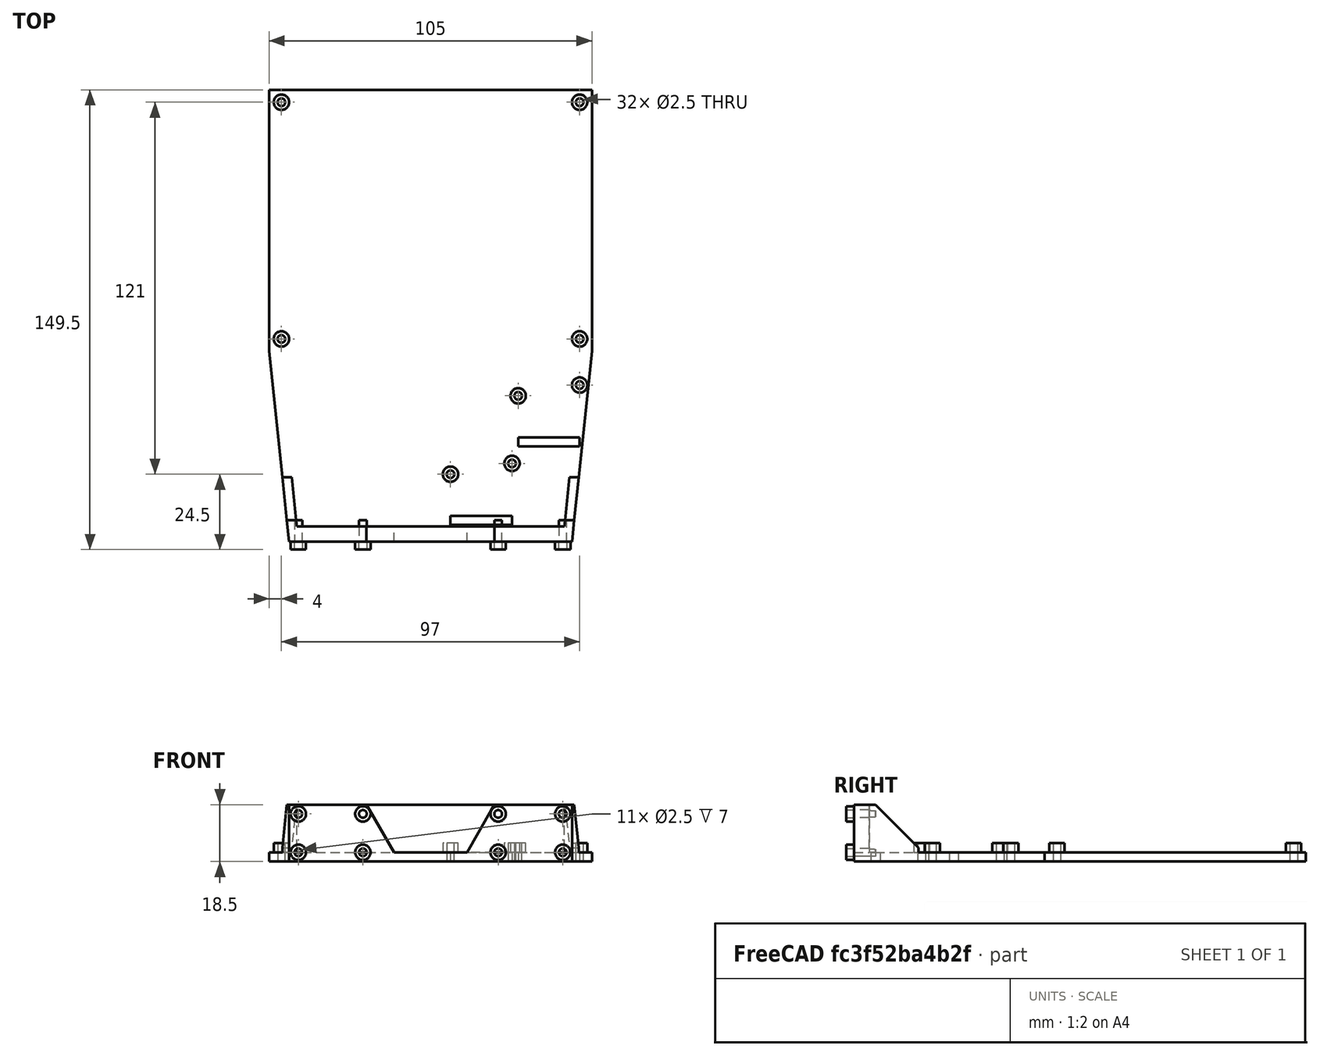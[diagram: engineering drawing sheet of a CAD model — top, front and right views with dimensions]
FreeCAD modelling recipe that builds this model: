
FCSTD DOCUMENT  (FreeCAD 0.17R8469 (Git))
Label: StereoVisionTest
License: All rights reserved
LicenseURL: http://en.wikipedia.org/wiki/All_rights_reserved
objects: Sketcher::SketchObject×7, PartDesign::Pad×4, PartDesign::Pocket×3, PartDesign::Chamfer×2, PartDesign::Body×2, App::Part×1
note: 25 computed .brp shape members not serialized (recipe doc carries the construction recipe); baked Part::Feature solids carry a one-line shape summary decoded from their .brp

FEATURE [Sketcher::SketchObject] Sketch
  MapMode = 5
  Support = -> [XY_Plane]
  sketch-geometry (36):
    g0: LineSegment StartX=0 StartY=0 StartZ=0 EndX=105 EndY=0 EndZ=0
    g1: LineSegment StartX=105 StartY=0 StartZ=0 EndX=105 EndY=-85 EndZ=0
    g2: LineSegment StartX=0 StartY=-85 StartZ=0 EndX=0 EndY=0 EndZ=0
    g3: LineSegment StartX=6.5 StartY=-147 StartZ=0 EndX=98.5 EndY=-147 EndZ=0
    g4: LineSegment StartX=6.5 StartY=-147 StartZ=0 EndX=0 EndY=-85 EndZ=0
    g5: LineSegment StartX=98.5 StartY=-147 StartZ=0 EndX=105 EndY=-85 EndZ=0
    g6: LineSegment [constr] StartX=105 StartY=-85 StartZ=0 EndX=0 EndY=-85 EndZ=0
    g7: LineSegment [constr] StartX=6.5 StartY=-85 StartZ=0 EndX=6.5 EndY=-147 EndZ=0
    g8: Circle CenterX=4 CenterY=-4 CenterZ=0 NormalX=0 NormalY=0 NormalZ=1 Radius=1.25
    g9: Circle CenterX=101 CenterY=-4 CenterZ=0 NormalX=0 NormalY=0 NormalZ=1 Radius=1.25
    g10: Circle CenterX=4 CenterY=-81 CenterZ=0 NormalX=0 NormalY=0 NormalZ=1 Radius=1.25
    g11: Circle CenterX=101 CenterY=-81 CenterZ=0 NormalX=0 NormalY=0 NormalZ=1 Radius=1.25
    g12: Circle CenterX=59 CenterY=-125 CenterZ=0 NormalX=0 NormalY=0 NormalZ=1 Radius=1.25
    g13: Circle CenterX=79 CenterY=-121.5 CenterZ=0 NormalX=0 NormalY=0 NormalZ=1 Radius=1.25
    g14: Circle CenterX=81 CenterY=-99.5 CenterZ=0 NormalX=0 NormalY=0 NormalZ=1 Radius=1.25
    g15: Circle CenterX=101 CenterY=-96 CenterZ=0 NormalX=0 NormalY=0 NormalZ=1 Radius=1.25
    g16: LineSegment [constr] StartX=4 StartY=-4 StartZ=0 EndX=101 EndY=-4 EndZ=0
    g17: LineSegment [constr] StartX=101 StartY=-4 StartZ=0 EndX=101 EndY=-81 EndZ=0
    g18: LineSegment [constr] StartX=101 StartY=-81 StartZ=0 EndX=4 EndY=-81 EndZ=0
    g19: LineSegment [constr] StartX=4 StartY=-81 StartZ=0 EndX=4 EndY=-4 EndZ=0
    g20: LineSegment [constr] StartX=59 StartY=-125 StartZ=0 EndX=79 EndY=-125 EndZ=0
    g21: LineSegment [constr] StartX=79 StartY=-125 StartZ=0 EndX=79 EndY=-121.5 EndZ=0
    g22: LineSegment [constr] StartX=79 StartY=-121.5 StartZ=0 EndX=59 EndY=-121.5 EndZ=0
    g23: LineSegment [constr] StartX=59 StartY=-121.5 StartZ=0 EndX=59 EndY=-125 EndZ=0
    g24: LineSegment [constr] StartX=81 StartY=-99.5 StartZ=0 EndX=101 EndY=-99.5 EndZ=0
    g25: LineSegment [constr] StartX=101 StartY=-99.5 StartZ=0 EndX=101 EndY=-96 EndZ=0
    g26: LineSegment [constr] StartX=101 StartY=-96 StartZ=0 EndX=81 EndY=-96 EndZ=0
    g27: LineSegment [constr] StartX=81 StartY=-96 StartZ=0 EndX=81 EndY=-99.5 EndZ=0
    g28: LineSegment [constr] StartX=0 StartY=0 StartZ=0 EndX=4 EndY=-4 EndZ=0
    g29: LineSegment [constr] StartX=105 StartY=0 StartZ=0 EndX=101 EndY=-4 EndZ=0
    g30: LineSegment [constr] StartX=101 StartY=-81 StartZ=0 EndX=101 EndY=-96 EndZ=0
    g31: LineSegment [constr] StartX=81 StartY=-99.5 StartZ=0 EndX=79 EndY=-99.5 EndZ=0
    g32: LineSegment [constr] StartX=79 StartY=-99.5 StartZ=0 EndX=79 EndY=-121.5 EndZ=0
    g33: LineSegment [constr] StartX=79 StartY=-121.5 StartZ=0 EndX=81 EndY=-121.5 EndZ=0
    g34: LineSegment [constr] StartX=81 StartY=-121.5 StartZ=0 EndX=81 EndY=-99.5 EndZ=0
    g35: LineSegment [constr] StartX=59 StartY=-125 StartZ=0 EndX=59 EndY=-147 EndZ=0
  constraints (89):
    c: Coincident(g0,g1)
    c: Coincident(g2,g0)
    c: Horizontal(g0)
    c: Vertical(g1)
    c: Vertical(g2)
    c: DistanceX(g0,g0) = 105
    c: DistanceY(g1,g1) = 85
    c: Coincident(g0,g-1)
    c: Horizontal(g3)
    c: DistanceX(g3,g3) = 92
    c: Coincident(g4,g3)
    c: Coincident(g5,g3)
    c: Coincident(g5,g1)
    c: Equal(g5,g4)
    c: Coincident(g4,g2)
    c: Coincident(g6,g1)
    c: Coincident(g6,g2)
    c: Horizontal(g6)
    c: PointOnObject(g7,g6)
    c: PointOnObject(g7,g3)
    c: Vertical(g7)
    c: Coincident(g3,g7)
    c: Radius(g8) = 1.25
    c: Equal(g8, g10-g15) x6
    c: Equal(g8,g9)
    c: Coincident(g16,g17)
    c: Coincident(g17,g18)
    c: Coincident(g18,g19)
    c: Coincident(g19,g16)
    c: Horizontal(g16)
    c: Horizontal(g18)
    c: Vertical(g17)
    c: Vertical(g19)
    c: Coincident(g20,g21)
    c: Coincident(g21,g22)
    c: Coincident(g22,g23)
    c: Coincident(g23,g20)
    c: Horizontal(g20)
    c: Horizontal(g22)
    c: Vertical(g21)
    c: Vertical(g23)
    c: Coincident(g24,g25)
    c: Coincident(g25,g26)
    c: Coincident(g26,g27)
    c: Coincident(g27,g24)
    c: Horizontal(g24)
    c: Horizontal(g26)
    c: Vertical(g25)
    c: Vertical(g27)
    c: Coincident(g8,g16)
    c: Coincident(g10,g18)
    c: Coincident(g9,g16)
    c: Coincident(g17,g11)
    c: Coincident(g20,g12)
    c: Coincident(g13,g21)
    c: Coincident(g24,g14)
    c: Coincident(g25,g15)
    c: Equal(g26,g22)
    c: Equal(g25,g21)
    c: DistanceX(g22,g22) = 20
    c: DistanceY(g21,g21) = 3.5
    c: DistanceY(g17,g17) = 77
    c: DistanceX(g18,g18) = 97
    c: Coincident(g28,g-1)
    c: Coincident(g28,g8)
    c: Coincident(g29,g0)
    c: Coincident(g29,g9)
    c: Equal(g29,g28)
    c: Angle(g28) = -0.785398
    c: Coincident(g30,g11)
    c: Coincident(g30,g15)
    c: Vertical(g30)
    c: Distance(g30) = 15
    c: Coincident(g31,g32)
    c: Coincident(g32,g33)
    c: Coincident(g33,g34)
    c: Coincident(g34,g31)
    c: Horizontal(g31)
    c: Horizontal(g33)
    c: Vertical(g32)
    c: Vertical(g34)
    c: Coincident(g31,g14)
    c: Coincident(g32,g13)
    c: Distance(g34) = 22
    c: Distance(g31) = 2
    c: Coincident(g35,g12)
    c: PointOnObject(g35,g3)
    c: Vertical(g35)
    c: Distance(g35) = 22
FEATURE [PartDesign::Pad] Pad
  Length = 3
  Length2 = 100
  Profile = -> Sketch
  Type = 0
FEATURE [Sketcher::SketchObject] Sketch001
  ExternalGeometry = -> [Pad]
  MapMode = 5
  Placement = pos=(0,0,3) rot=(0,0,1;0rad)
  Support = -> [Pad]
  sketch-geometry (16):
    g0: Circle CenterX=4 CenterY=-4 CenterZ=0 NormalX=0 NormalY=0 NormalZ=1 Radius=2.5
    g1: Circle CenterX=101 CenterY=-81 CenterZ=0 NormalX=0 NormalY=0 NormalZ=1 Radius=2.5
    g2: Circle CenterX=101 CenterY=-4 CenterZ=0 NormalX=0 NormalY=0 NormalZ=1 Radius=2.5
    g3: Circle CenterX=4 CenterY=-81 CenterZ=0 NormalX=0 NormalY=0 NormalZ=1 Radius=2.5
    g4: Circle CenterX=79 CenterY=-121.5 CenterZ=0 NormalX=0 NormalY=0 NormalZ=1 Radius=2.5
    g5: Circle CenterX=59 CenterY=-125 CenterZ=0 NormalX=0 NormalY=0 NormalZ=1 Radius=2.5
    g6: Circle CenterX=81 CenterY=-99.5 CenterZ=0 NormalX=0 NormalY=0 NormalZ=1 Radius=2.5
    g7: Circle CenterX=101 CenterY=-96 CenterZ=0 NormalX=0 NormalY=0 NormalZ=1 Radius=1.25
    g8: Circle CenterX=4 CenterY=-81 CenterZ=0 NormalX=0 NormalY=0 NormalZ=1 Radius=1.25
    g9: Circle CenterX=79 CenterY=-121.5 CenterZ=0 NormalX=0 NormalY=0 NormalZ=1 Radius=1.25
    g10: Circle CenterX=81 CenterY=-99.5 CenterZ=0 NormalX=0 NormalY=0 NormalZ=1 Radius=1.25
    g11: Circle CenterX=101 CenterY=-96 CenterZ=0 NormalX=0 NormalY=0 NormalZ=1 Radius=2.5
    g12: Circle CenterX=59 CenterY=-125 CenterZ=0 NormalX=0 NormalY=0 NormalZ=1 Radius=1.25
    g13: Circle CenterX=101 CenterY=-4 CenterZ=0 NormalX=0 NormalY=0 NormalZ=1 Radius=1.25
    g14: Circle CenterX=4 CenterY=-4 CenterZ=0 NormalX=0 NormalY=0 NormalZ=1 Radius=1.25
    g15: Circle CenterX=101 CenterY=-81 CenterZ=0 NormalX=0 NormalY=0 NormalZ=1 Radius=1.25
  constraints (27):
    c: Coincident(g6,g-8)
    c: Coincident(g7,g-9)
    c: Coincident(g5,g-10)
    c: Coincident(g4,g-7)
    c: Coincident(g3,g-6)
    c: Coincident(g2,g-5)
    c: Coincident(g1,g-3)
    c: Coincident(g0,g-4)
    c: Radius(g0) = 2.5
    c: Equal(g0, g1-g6) x6
    c: Coincident(g8,g3)
    c: Equal(g8,g-6)
    c: Coincident(g9,g4)
    c: Equal(g9,g-7)
    c: Coincident(g10,g6)
    c: Equal(g10,g-8)
    c: Coincident(g11,g7)
    c: Coincident(g12,g5)
    c: Equal(g12,g-10)
    c: Coincident(g13,g2)
    c: Equal(g13,g-5)
    c: Coincident(g14,g0)
    c: Equal(g14,g-4)
    c: Coincident(g15,g1)
    c: Equal(g15,g-3)
    c: Equal(g11,g0)
    c: Equal(g7,g-9)
FEATURE [PartDesign::Pad] Pad001
  BaseFeature = -> Pad
  Length = 3
  Length2 = 100
  Profile = -> Sketch001
  Type = 0
FEATURE [Sketcher::SketchObject] Sketch002
  ExternalGeometry = -> [Pad001]
  MapMode = 5
  Placement = pos=(0,0,3) rot=(0,0,1;0rad)
  Support = -> [Pad001]
  sketch-geometry (13):
    g0: LineSegment StartX=6.5 StartY=-147 StartZ=0 EndX=98.5 EndY=-147 EndZ=0
    g1: LineSegment StartX=98.5 StartY=-147 StartZ=0 EndX=100.702 EndY=-126 EndZ=0
    g2: LineSegment StartX=6.5 StartY=-147 StartZ=0 EndX=4.29839 EndY=-126 EndZ=0
    g3: LineSegment [constr] StartX=4.29839 StartY=-126 StartZ=0 EndX=100.702 EndY=-126 EndZ=0
    g4: LineSegment [constr] StartX=4 StartY=-81 StartZ=0 EndX=4 EndY=-126 EndZ=0
    g5: LineSegment StartX=8.99225 StartY=-142 StartZ=0 EndX=96.0078 EndY=-142 EndZ=0
    g6: LineSegment StartX=96.0078 StartY=-142 StartZ=0 EndX=97.6852 EndY=-126 EndZ=0
    g7: LineSegment StartX=8.99225 StartY=-142 StartZ=0 EndX=7.31483 EndY=-126 EndZ=0
    g8: LineSegment StartX=4.29839 StartY=-126 StartZ=0 EndX=7.31483 EndY=-126 EndZ=0
    g9: LineSegment StartX=97.6852 StartY=-126 StartZ=0 EndX=100.702 EndY=-126 EndZ=0
    g10: LineSegment [constr] StartX=96.0078 StartY=-142 StartZ=0 EndX=98.9914 EndY=-142.313 EndZ=0
    g11: LineSegment [constr] StartX=96.0078 StartY=-142 StartZ=0 EndX=96.0078 EndY=-147 EndZ=0
    g12: LineSegment [constr] StartX=8.99225 StartY=-142 StartZ=0 EndX=6.0086 EndY=-142.313 EndZ=0
  constraints (36):
    c: Coincident(g0,g-5)
    c: Coincident(g0,g-4)
    c: Coincident(g1,g0)
    c: PointOnObject(g1,g-3)
    c: Coincident(g2,g0)
    c: PointOnObject(g2,g-5)
    c: Coincident(g3,g2)
    c: Coincident(g3,g1)
    c: Horizontal(g3)
    c: Coincident(g4,g-6)
    c: PointOnObject(g4,g3)
    c: Vertical(g4)
    c: DistanceY(g4,g4) = 45
    c: Horizontal(g5)
    c: Coincident(g6,g5)
    c: PointOnObject(g6,g3)
    c: Coincident(g7,g5)
    c: PointOnObject(g7,g3)
    c: Parallel(g7,g-5)
    c: Parallel(g6,g-3)
    c: Coincident(g8,g2)
    c: Coincident(g8,g7)
    c: Coincident(g9,g6)
    c: Coincident(g9,g1)
    c: Coincident(g10,g5)
    c: Coincident(g11,g5)
    c: PointOnObject(g11,g-4)
    c: Vertical(g11)
    c: Perpendicular(g-3,g10)
    c: PointOnObject(g10,g-3)
    c: DistanceY(g11,g11) = 5
    c: Distance(g10) = 3
    c: Coincident(g12,g5)
    c: PointOnObject(g12,g-5)
    c: Perpendicular(g-5,g12)
    c: Distance(g12) = 3
FEATURE [PartDesign::Pad] Pad002
  BaseFeature = -> Pad001
  Length = 15.5
  Length2 = 100
  Profile = -> Sketch002
  Type = 0
FEATURE [PartDesign::Chamfer] Chamfer
  Base = -> Pad002 [Edge82]
  BaseFeature = -> Pad002
  Size = 14
FEATURE [PartDesign::Chamfer] Chamfer001
  Base = -> Chamfer [Edge11]
  BaseFeature = -> Chamfer
  Size = 14
FEATURE [Sketcher::SketchObject] Sketch003
  ExternalGeometry = -> [Chamfer001]
  MapMode = 5
  Placement = pos=(0,-147,0) rot=(1,0,0;1.5708rad)
  Support = -> [Chamfer001]
  sketch-geometry (20):
    g0: LineSegment [constr] StartX=9.5 StartY=15.5 StartZ=0 EndX=30.5 EndY=15.5 EndZ=0
    g1: LineSegment [constr] StartX=30.5 StartY=15.5 StartZ=0 EndX=30.5 EndY=3 EndZ=0
    g2: LineSegment [constr] StartX=30.5 StartY=3 StartZ=0 EndX=9.5 EndY=3 EndZ=0
    g3: LineSegment [constr] StartX=9.5 StartY=3 StartZ=0 EndX=9.5 EndY=15.5 EndZ=0
    g4: LineSegment [constr] StartX=74.5 StartY=15.5 StartZ=0 EndX=95.5 EndY=15.5 EndZ=0
    g5: LineSegment [constr] StartX=95.5 StartY=15.5 StartZ=0 EndX=95.5 EndY=3 EndZ=0
    g6: LineSegment [constr] StartX=95.5 StartY=3 StartZ=0 EndX=74.5 EndY=3 EndZ=0
    g7: LineSegment [constr] StartX=74.5 StartY=3 StartZ=0 EndX=74.5 EndY=15.5 EndZ=0
    g8: LineSegment [constr] StartX=30.5 StartY=15.5 StartZ=0 EndX=74.5 EndY=15.5 EndZ=0
    g9: LineSegment [constr] StartX=6.5 StartY=18.5 StartZ=0 EndX=9.5 EndY=15.5 EndZ=0
    g10: LineSegment [constr] StartX=95.5 StartY=15.5 StartZ=0 EndX=98.5 EndY=18.5 EndZ=0
    g11: LineSegment [constr] StartX=9.5 StartY=3 StartZ=0 EndX=9.5 EndY=0 EndZ=0
    g12: Circle CenterX=9.5 CenterY=15.5 CenterZ=0 NormalX=0 NormalY=0 NormalZ=1 Radius=1.25
    g13: Circle CenterX=30.5 CenterY=15.5 CenterZ=0 NormalX=0 NormalY=0 NormalZ=1 Radius=1.25
    g14: Circle CenterX=9.5 CenterY=3 CenterZ=0 NormalX=0 NormalY=0 NormalZ=1 Radius=1.25
    g15: Circle CenterX=30.5 CenterY=3 CenterZ=0 NormalX=0 NormalY=0 NormalZ=1 Radius=1.25
    g16: Circle CenterX=74.5 CenterY=3 CenterZ=0 NormalX=0 NormalY=0 NormalZ=1 Radius=1.25
    g17: Circle CenterX=95.5 CenterY=3 CenterZ=0 NormalX=0 NormalY=0 NormalZ=1 Radius=1.25
    g18: Circle CenterX=95.5 CenterY=15.5 CenterZ=0 NormalX=0 NormalY=0 NormalZ=1 Radius=1.25
    g19: Circle CenterX=74.5 CenterY=15.5 CenterZ=0 NormalX=0 NormalY=0 NormalZ=1 Radius=1.25
  constraints (49):
    c: Coincident(g0,g1)
    c: Coincident(g1,g2)
    c: Coincident(g2,g3)
    c: Coincident(g3,g0)
    c: Horizontal(g0)
    c: Horizontal(g2)
    c: Vertical(g1)
    c: Vertical(g3)
    c: Coincident(g4,g5)
    c: Coincident(g5,g6)
    c: Coincident(g6,g7)
    c: Coincident(g7,g4)
    c: Horizontal(g4)
    c: Horizontal(g6)
    c: Vertical(g5)
    c: Vertical(g7)
    c: Coincident(g8,g0)
    c: Coincident(g8,g4)
    c: Horizontal(g8)
    c: DistanceX(g8,g8) = 44
    c: Equal(g4,g0)
    c: Equal(g5,g1)
    c: DistanceY(g5,g5) = 12.5
    c: DistanceX(g4,g4) = 21
    c: Coincident(g9,g-3)
    c: Coincident(g9,g0)
    c: Coincident(g10,g4)
    c: Coincident(g10,g-3)
    c: Equal(g10,g9)
    c: Coincident(g11,g2)
    c: PointOnObject(g11,g-4)
    c: Vertical(g11)
    c: DistanceY(g11,g11) = 3
    c: Coincident(g12,g0)
    c: Coincident(g13,g0)
    c: Coincident(g14,g2)
    c: Coincident(g15,g1)
    c: Coincident(g16,g6)
    c: Coincident(g17,g5)
    c: Coincident(g18,g4)
    c: Coincident(g19,g4)
    c: Radius(g14) = 1.25
    c: Equal(g14,g12)
    c: Equal(g14,g13)
    c: Equal(g14,g15)
    c: Equal(g14,g16)
    c: Equal(g14,g19)
    c: Equal(g14,g17)
    c: Equal(g14,g18)
FEATURE [PartDesign::Pocket] Pocket
  BaseFeature = -> Chamfer001
  Length = 7
  Profile = -> Sketch003
  Type = 0
FEATURE [Sketcher::SketchObject] Sketch004
  ExternalGeometry = -> [Pocket]
  MapMode = 5
  Placement = pos=(0,-147,0) rot=(1,0,0;1.5708rad)
  Support = -> [Pocket]
  sketch-geometry (16):
    g0: Circle CenterX=9.5 CenterY=15.5 CenterZ=0 NormalX=0 NormalY=0 NormalZ=1 Radius=2.5
    g1: Circle CenterX=30.5 CenterY=15.5 CenterZ=0 NormalX=0 NormalY=0 NormalZ=1 Radius=2.5
    g2: Circle CenterX=74.5 CenterY=15.5 CenterZ=0 NormalX=0 NormalY=0 NormalZ=1 Radius=2.5
    g3: Circle CenterX=95.5 CenterY=15.5 CenterZ=0 NormalX=0 NormalY=0 NormalZ=1 Radius=2.5
    g4: Circle CenterX=95.5 CenterY=3 CenterZ=0 NormalX=0 NormalY=0 NormalZ=1 Radius=2.5
    g5: Circle CenterX=74.5 CenterY=3 CenterZ=0 NormalX=0 NormalY=0 NormalZ=1 Radius=2.5
    g6: Circle CenterX=30.5 CenterY=3 CenterZ=0 NormalX=0 NormalY=0 NormalZ=1 Radius=2.5
    g7: Circle CenterX=9.5 CenterY=3 CenterZ=0 NormalX=0 NormalY=0 NormalZ=1 Radius=2.5
    g8: Circle CenterX=9.5 CenterY=15.5 CenterZ=0 NormalX=0 NormalY=0 NormalZ=1 Radius=1.25
    g9: Circle CenterX=30.5 CenterY=15.5 CenterZ=0 NormalX=0 NormalY=0 NormalZ=1 Radius=1.25
    g10: Circle CenterX=9.5 CenterY=3 CenterZ=0 NormalX=0 NormalY=0 NormalZ=1 Radius=1.25
    g11: Circle CenterX=30.5 CenterY=3 CenterZ=0 NormalX=0 NormalY=0 NormalZ=1 Radius=1.25
    g12: Circle CenterX=74.5 CenterY=15.5 CenterZ=0 NormalX=0 NormalY=0 NormalZ=1 Radius=1.25
    g13: Circle CenterX=74.5 CenterY=3 CenterZ=0 NormalX=0 NormalY=0 NormalZ=1 Radius=1.25
    g14: Circle CenterX=95.5 CenterY=15.5 CenterZ=0 NormalX=0 NormalY=0 NormalZ=1 Radius=1.25
    g15: Circle CenterX=95.5 CenterY=3 CenterZ=0 NormalX=0 NormalY=0 NormalZ=1 Radius=1.25
  constraints (32):
    c: Coincident(g0,g-9)
    c: Coincident(g1,g-10)
    c: Coincident(g2,g-3)
    c: Coincident(g3,g-4)
    c: Coincident(g4,g-5)
    c: Coincident(g5,g-6)
    c: Coincident(g6,g-7)
    c: Coincident(g7,g-8)
    c: Radius(g0) = 2.5
    c: Equal(g0,g1)
    c: Equal(g0,g2)
    c: Equal(g0,g3)
    c: Equal(g0,g6)
    c: Equal(g0,g7)
    c: Equal(g0,g5)
    c: Equal(g0,g4)
    c: Coincident(g8,g0)
    c: Equal(g8,g-9)
    c: Coincident(g9,g1)
    c: Equal(g9,g-10)
    c: Coincident(g10,g7)
    c: Equal(g10,g-8)
    c: Coincident(g11,g6)
    c: Equal(g11,g-7)
    c: Coincident(g12,g2)
    c: Coincident(g13,g5)
    c: Coincident(g14,g3)
    c: Coincident(g15,g4)
    c: Equal(g15,g-5)
    c: Equal(g14,g-4)
    c: Equal(g13,g-6)
    c: Equal(g12,g-3)
FEATURE [PartDesign::Pad] Pad003
  BaseFeature = -> Pocket
  Length = 2.5
  Length2 = 100
  Profile = -> Sketch004
  Type = 0
FEATURE [PartDesign::Body] Body
  Origin = -> BodyOrigin
  Tip = -> Pad003
FEATURE [Sketcher::SketchObject] Sketch005
  ExternalGeometry = -> [Pad003]
  MapMode = 5
  Placement = pos=(0,-147,0) rot=(1,0,0;1.5708rad)
  Support = -> [Pad003]
  sketch-geometry (4):
    g0: LineSegment StartX=31.6547 StartY=18.5 StartZ=0 EndX=40.6036 EndY=3 EndZ=0
    g1: LineSegment StartX=73.3453 StartY=18.5 StartZ=0 EndX=64.3964 EndY=3 EndZ=0
    g2: LineSegment StartX=40.6036 StartY=3 StartZ=0 EndX=64.3964 EndY=3 EndZ=0
    g3: LineSegment StartX=73.3453 StartY=18.5 StartZ=0 EndX=31.6547 EndY=18.5 EndZ=0
  constraints (12):
    c: PointOnObject(g0,g-3)
    c: PointOnObject(g0,g-6)
    c: PointOnObject(g1,g-3)
    c: PointOnObject(g1,g-6)
    c: Coincident(g2,g0)
    c: Coincident(g2,g1)
    c: Coincident(g3,g1)
    c: Coincident(g3,g0)
    c: Tangent(g1,g-5)
    c: Tangent(g0,g-4)
    c: Angle(g1) = -2.0944
    c: Angle(g0) = -1.0472
FEATURE [PartDesign::Pocket] Pocket001
  BaseFeature = -> Pad003
  Length = 5
  Profile = -> Sketch005
  Type = 0
FEATURE [Sketcher::SketchObject] Sketch006
  ExternalGeometry = -> [Pocket001]
  MapMode = 5
  Placement = pos=(0,0,3) rot=(0,0,1;0rad)
  Support = -> [Pocket001]
  sketch-geometry (10):
    g0: LineSegment StartX=81 StartY=-113 StartZ=0 EndX=101 EndY=-113 EndZ=0
    g1: LineSegment StartX=101 StartY=-113 StartZ=0 EndX=101 EndY=-116 EndZ=0
    g2: LineSegment StartX=101 StartY=-116 StartZ=0 EndX=81 EndY=-116 EndZ=0
    g3: LineSegment StartX=81 StartY=-116 StartZ=0 EndX=81 EndY=-113 EndZ=0
    g4: LineSegment StartX=59 StartY=-138.5 StartZ=0 EndX=79 EndY=-138.5 EndZ=0
    g5: LineSegment StartX=79 StartY=-138.5 StartZ=0 EndX=79 EndY=-141.5 EndZ=0
    g6: LineSegment StartX=79 StartY=-141.5 StartZ=0 EndX=59 EndY=-141.5 EndZ=0
    g7: LineSegment StartX=59 StartY=-141.5 StartZ=0 EndX=59 EndY=-138.5 EndZ=0
    g8: LineSegment [constr] StartX=81 StartY=-99.5 StartZ=0 EndX=81 EndY=-113 EndZ=0
    g9: LineSegment [constr] StartX=59 StartY=-125 StartZ=0 EndX=59 EndY=-138.5 EndZ=0
  constraints (28):
    c: Coincident(g0,g1)
    c: Coincident(g1,g2)
    c: Coincident(g2,g3)
    c: Coincident(g3,g0)
    c: Horizontal(g0)
    c: Horizontal(g2)
    c: Vertical(g1)
    c: Vertical(g3)
    c: Coincident(g4,g5)
    c: Coincident(g5,g6)
    c: Coincident(g6,g7)
    c: Coincident(g7,g4)
    c: Horizontal(g4)
    c: Horizontal(g6)
    c: Vertical(g5)
    c: Vertical(g7)
    c: Equal(g4,g0)
    c: Equal(g5,g1)
    c: Distance(g4) = 20
    c: Distance(g5) = 3
    c: Coincident(g8,g-3)
    c: Coincident(g8,g0)
    c: Coincident(g9,g-5)
    c: Coincident(g9,g4)
    c: Vertical(g9)
    c: Vertical(g8)
    c: Equal(g8,g9)
    c: Distance(g9) = 13.5
FEATURE [PartDesign::Pocket] Pocket002
  BaseFeature = -> Pocket001
  Length = 5
  Profile = -> Sketch006
  Type = 0
FEATURE [PartDesign::Body] Pad003Body
  Model = -> [Sketch,Pad,Sketch001,Pad001,Sketch002,Pad002,Chamfer,Chamfer001,Sketch003,Pocket,Sketch004,Pad003,Sketch005,Pocket001,Sketch006,Pocket002]
  Origin = -> Pad003BodyOrigin
  Tip = -> Pocket002
FEATURE [App::Part] Part
  Group = -> [Pad003Body]
  License = CC BY 3.0
  LicenseURL = http://creativecommons.org/licenses/by/3.0/
  Origin = -> PartOrigin
